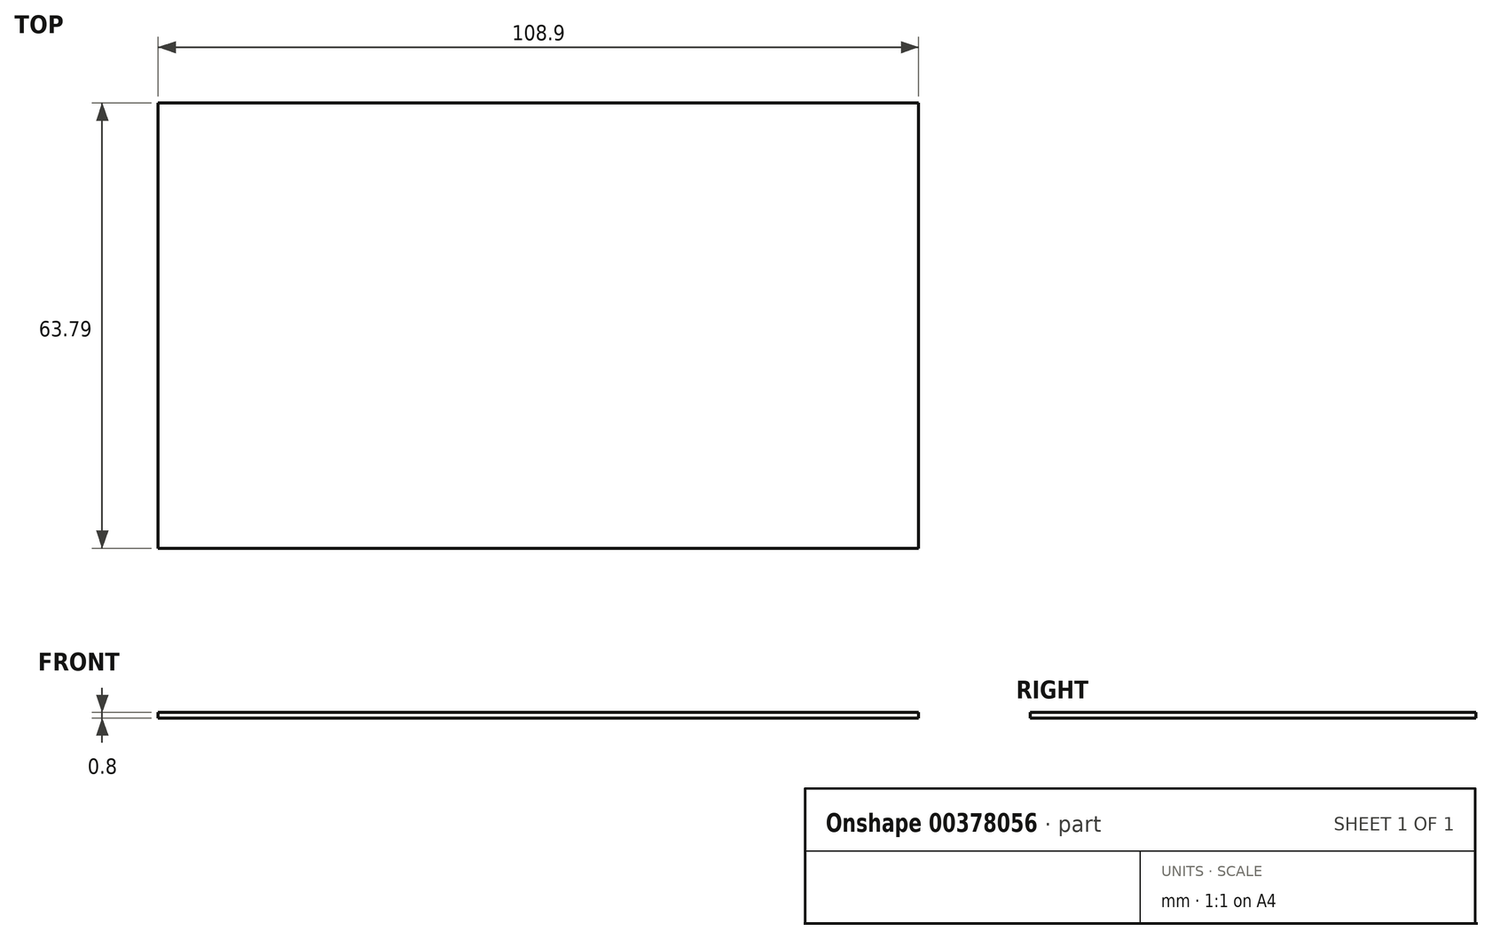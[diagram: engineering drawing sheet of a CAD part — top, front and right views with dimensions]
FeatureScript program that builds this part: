
annotation { "Feature Type Name" : "Feature", "Feature Type Description" : "" }
export const myFeature = defineFeature(function(context is Context, id is Id, definition is map)
    precondition{}
    {
        {
            var Q0;
            Q0=qCreatedBy(makeId("Top.planeOp"),FACE);
            var sketch = newSketch(context, id + "F0", { "sketchPlane" : qUnion([Q0])});
            skLineSegment(sketch, "E0.bottom", {"start": v(-53.78, -31.56) * mm, "end": v(55.12, -31.56) * mm});
            skLineSegment(sketch, "E0.top", {"start": v(-53.78, 32.23) * mm, "end": v(55.12, 32.23) * mm});
            skLineSegment(sketch, "E0.left", {"start": v(-53.78, -31.56) * mm, "end": v(-53.78, 32.23) * mm});
            skLineSegment(sketch, "E0.right", {"start": v(55.12, -31.56) * mm, "end": v(55.12, 32.23) * mm});
            skSolve(sketch);
        }
        {
            var Q0;
            Q0=makeQuery(id+"F0.imprint","IMPRINT",FACE,{"disambiguationData":[TD([[makeQuery(id+"F0.imprint","IMPRINT",EDGE,{"derivedFrom":sQuery(id+"F0.wireOp",EDGE,"E0.bottom")}),1.0]])]});
            extrude(context, id + "F1", {"entities" : qUnion([Q0]), "depth" : 0.8 * mm});
        }
    });
